# Revit family: EKF_EE_ДверьГлухаяTrivia_AVERES
name_source: partatom
category: Электрооборудование
units: mm (PartAtom-declared; Revit-internal decimal feet)

## family parameters
Всегда вертикально = Нет
На основе рабочей плоскости = Да
Общий = Да
При загрузке вырезать с полостями = Нет
Размер круглого соединителя = Использовать диаметр
Тип детали = Силовой щит
Точка расчета площади = Нет

## types (8) — shared parameters
ADSK_Единица измерения = шт.
ADSK_Завод-изготовитель = EKF
ADSK_Количество = 1
ADSK_Марка = Дверь глухая металлическая
ADSK_Материал = RAL 7035_Сталь
ADSK_Обозначение = Дверь глухая металлическая
ADSK_Размер_Высота = 2013 мм
ADSK_Размер_Глубина = 30 мм
Изготовитель = EKF
Карман для документации = Да
КолОтв = 4
Отметка по умолчанию = 1219.2 мм
Серия номенклатуры = Averes
ТВ = EKF_2_TRIVIA_AVERES
Тип установки = -
ТипДверцы = Вл_ДверцаГлухая
zero-valued in all types: ADSK_Масса

## per-type parameters (varying)
| type | ADSK_Код изделия | ADSK_Размер_Ширина | Степень защиты IP | Тип |
| Дверь глухая металлическая Ш300 IP30 EKF AVERES | D2M300 | 300 мм | IP30 | 408 мм |
| Дверь глухая металлическая Ш300 IP55 EKF AVERES | D2M300WP | 300 мм | IP55 | 409 мм |
| Дверь глухая металлическая Ш400 IP30 EKF AVERES | D2M400 | 400 мм | IP30 | 410 мм |
| Дверь глухая металлическая Ш400 IP55 EKF AVERES | D2M400WP | 400 мм | IP55 | 411 мм |
| Дверь глухая металлическая Ш600 IP30 EKF AVERES | D2M600 | 600 мм | IP30 | 412 мм |
| Дверь глухая металлическая Ш600 IP55 EKF AVERES | D2M600WP | 600 мм | IP55 | 413 мм |
| Дверь глухая металлическая Ш800 IP30 EKF AVERES | D2M800 | 800 мм | IP30 | 414 мм |
| Дверь глухая металлическая Ш800 IP55 EKF AVERES | D2M800WP | 800 мм | IP55 | 415 мм |

note: column(s) folded — value = type name in every type: ADSK_Наименование
